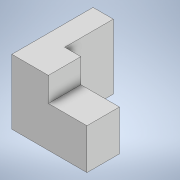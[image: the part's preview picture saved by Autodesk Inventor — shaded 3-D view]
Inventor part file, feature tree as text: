
AUTODESK INVENTOR PART (.ipt)
format: ipt  version: 2021 (Build 250183000, 183)  size: 111,104 bytes
history: native  units: mm
features: sketch x5, extrude x3
ambient origin geometry x8: Origin, YZ Plane, XZ Plane, XY Plane, X Axis, Y Axis, Z Axis, Center Point
bodies: Solid1 (feature_tree)
feature tree (8):
  sketch  "Sketch1"  dims[d0=32.0mm d1=40.0mm]
  extrude  "Extrusion1"  Depth=40.0mm
  sketch  "Sketch3"  dims[d5=8.0mm d6=0.0mm d7=16.0mm]
  extrude  "Extrusion2"  Depth=16.0mm
  extrude  "Extrusion3"  Depth=16.0mm
  sketch  "Sketch2"  dims[d2=10.0mm d3=0.0mm d4=16.0mm]
  sketch  "Sketch4"  dims[d8=20.0mm]
  sketch  "Sketch5"  dims[d9=19.0mm d10=0.0mm]
